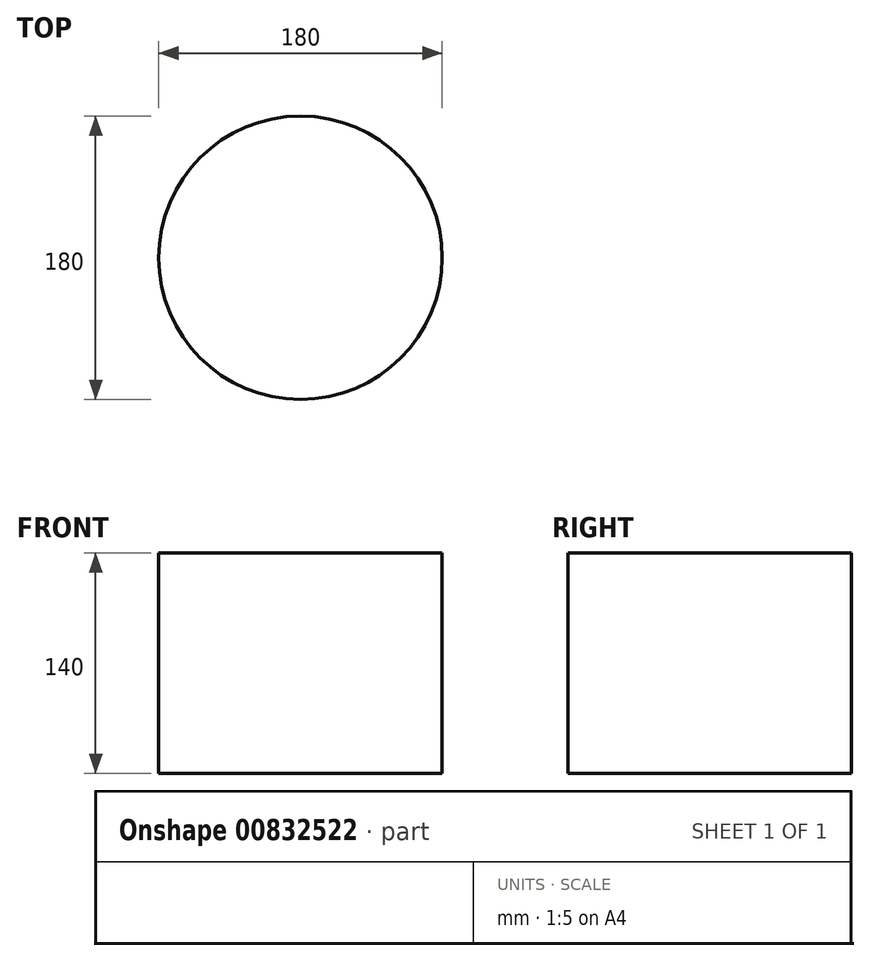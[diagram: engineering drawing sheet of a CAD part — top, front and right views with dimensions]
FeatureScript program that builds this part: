
annotation { "Feature Type Name" : "Feature", "Feature Type Description" : "" }
export const myFeature = defineFeature(function(context is Context, id is Id, definition is map)
    precondition{}
    {
        {
            var Q0;
            Q0=qCreatedBy(makeId("Top.planeOp"),FACE);
            var sketch = newSketch(context, id + "F0", { "sketchPlane" : qUnion([Q0])});
            skCircle(sketch, "E0", {"center": v(0, 0) * mm, "radius": 90 * mm});
            skSolve(sketch);
        }
        {
            var Q0;
            Q0=sQuery(id+"F0.wireOp",EDGE,"E0");
            extrude(context, id + "F1", {"bodyType" : ToolBodyType.SURFACE, "surfaceEntities" : qUnion([Q0]), "depth" : 140 * mm, "offsetDistance" : 25 * mm});
        }
    });
